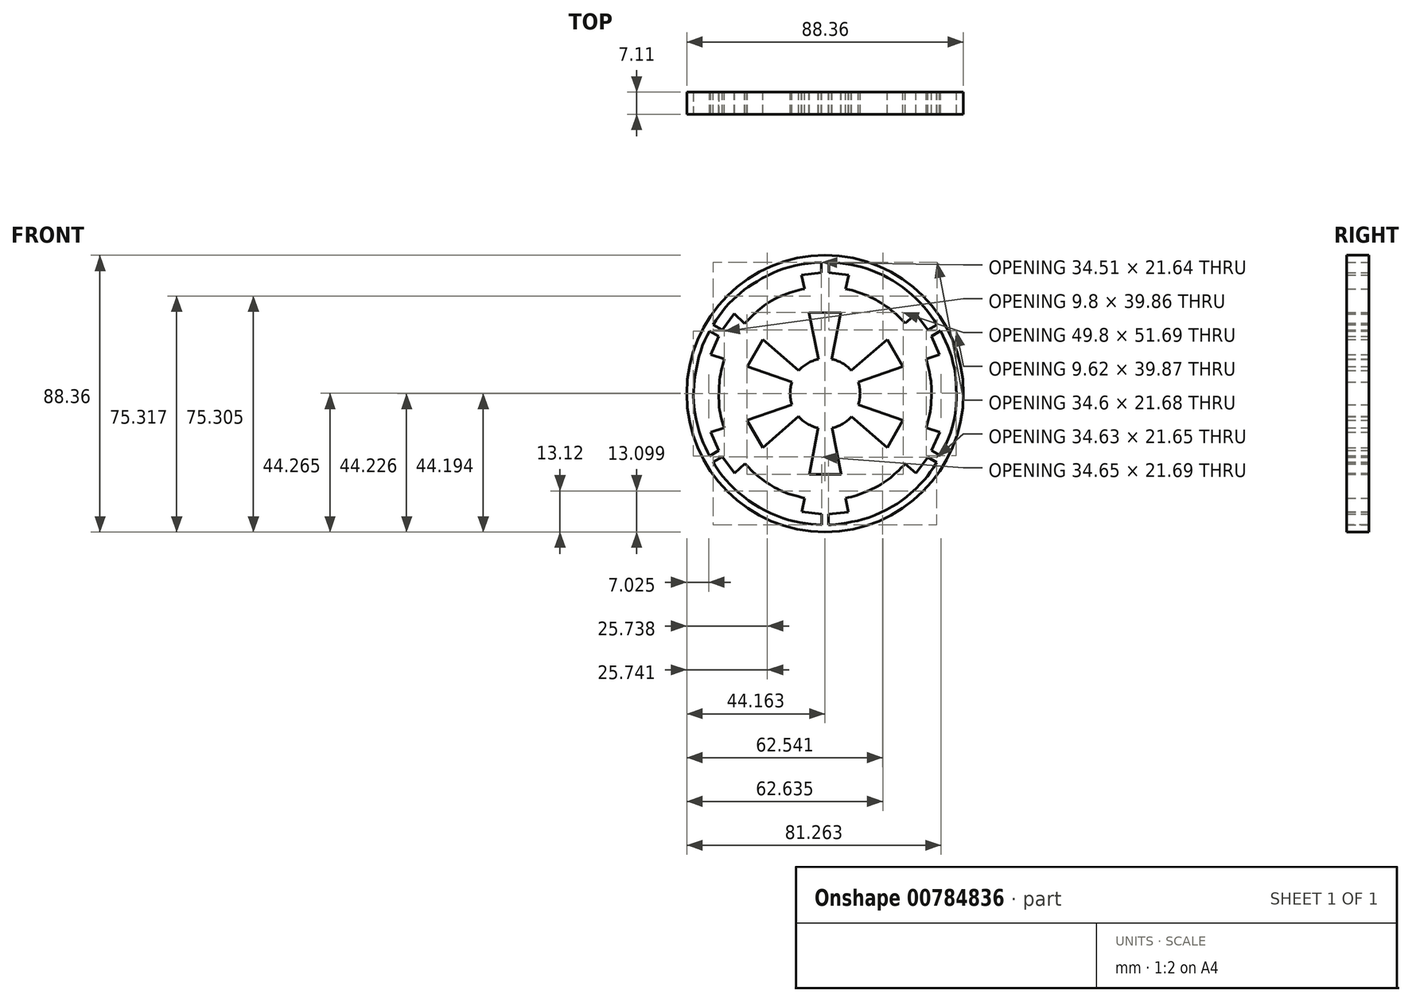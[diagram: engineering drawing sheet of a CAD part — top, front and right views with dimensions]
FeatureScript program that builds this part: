
annotation { "Feature Type Name" : "Feature", "Feature Type Description" : "" }
export const myFeature = defineFeature(function(context is Context, id is Id, definition is map)
    precondition{}
    {
        {
            var Q0;
            Q0=qCreatedBy(makeId("Front.planeOp"),FACE);
            var sketch = newSketch(context, id + "F0", { "sketchPlane" : qUnion([Q0])});
            skLineSegment(sketch, "E0", {"start": v(2.62, -13.26) * mm, "end": v(5.1, -25.8) * mm});
            skLineSegment(sketch, "E1", {"start": v(-2.6, -13.26) * mm, "end": v(-4.96, -25.83) * mm});
            skLineSegment(sketch, "E2", {"start": v(-4.96, -25.83) * mm, "end": v(5.1, -25.8) * mm});
            skLineSegment(sketch, "E3", {"start": v(-10.25, -8.8) * mm, "end": v(-19.88, -17.27) * mm});
            skLineSegment(sketch, "E4", {"start": v(-12.81, -4.3) * mm, "end": v(-24.92, -8.51) * mm});
            skLineSegment(sketch, "E5", {"start": v(-24.92, -8.51) * mm, "end": v(-19.88, -17.27) * mm});
            skLineSegment(sketch, "E6", {"start": v(12.8, -4.3) * mm, "end": v(24.88, -8.51) * mm});
            skLineSegment(sketch, "E7", {"start": v(10.2, -8.87) * mm, "end": v(19.9, -17.2) * mm});
            skLineSegment(sketch, "E8", {"start": v(19.9, -17.2) * mm, "end": v(24.88, -8.51) * mm});
            skLineSegment(sketch, "E9", {"start": v(12.77, 4.44) * mm, "end": v(24.88, 8.63) * mm});
            skLineSegment(sketch, "E10", {"start": v(10.14, 8.94) * mm, "end": v(19.81, 17.33) * mm});
            skLineSegment(sketch, "E11", {"start": v(19.81, 17.33) * mm, "end": v(24.88, 8.63) * mm});
            skLineSegment(sketch, "E12", {"start": v(2.56, 13.27) * mm, "end": v(5.03, 25.86) * mm});
            skLineSegment(sketch, "E13", {"start": v(-2.57, 13.27) * mm, "end": v(-5.14, 25.83) * mm});
            skLineSegment(sketch, "E14", {"start": v(-5.14, 25.83) * mm, "end": v(5.03, 25.86) * mm});
            skLineSegment(sketch, "E15", {"start": v(-10.19, 8.88) * mm, "end": v(-19.85, 17.32) * mm});
            skLineSegment(sketch, "E16", {"start": v(-12.77, 4.43) * mm, "end": v(-24.88, 8.62) * mm});
            skLineSegment(sketch, "E17", {"start": v(-24.88, 8.62) * mm, "end": v(-19.85, 17.32) * mm});
            skLineSegment(sketch, "E18", {"start": v(-1.19, 41.94) * mm, "end": v(-1.19, 38.6) * mm});
            skLineSegment(sketch, "E19", {"start": v(1.15, 41.98) * mm, "end": v(1.15, 38.6) * mm});
            skLineSegment(sketch, "E20", {"start": v(34, 18.3) * mm, "end": v(36.91, 20.02) * mm});
            skLineSegment(sketch, "E21", {"start": v(34, -18.17) * mm, "end": v(36.9, -19.85) * mm});
            skLineSegment(sketch, "E22", {"start": v(32.88, -20.26) * mm, "end": v(35.68, -21.93) * mm});
            skLineSegment(sketch, "E23", {"start": v(-32.81, -20.21) * mm, "end": v(-35.76, -21.87) * mm});
            skLineSegment(sketch, "E24", {"start": v(-36.86, -19.88) * mm, "end": v(-33.93, -18.2) * mm});
            skLineSegment(sketch, "E25", {"start": v(-36.87, 19.98) * mm, "end": v(-33.92, 18.32) * mm});
            skLineSegment(sketch, "E26", {"start": v(-35.7, 22.04) * mm, "end": v(-32.8, 20.3) * mm});
            skLineSegment(sketch, "E27", {"start": v(-33.92, 18.32) * mm, "end": v(-36.56, 12.47) * mm});
            skLineSegment(sketch, "E28", {"start": v(-36.56, 12.47) * mm, "end": v(-32.26, 11.04) * mm});
            skLineSegment(sketch, "E29", {"start": v(-32.8, 20.3) * mm, "end": v(-29, 25.5) * mm});
            skLineSegment(sketch, "E30", {"start": v(-29, 25.5) * mm, "end": v(-25.68, 22.43) * mm});
            skLineSegment(sketch, "E31", {"start": v(-33.93, -18.2) * mm, "end": v(-36.55, -12.33) * mm});
            skLineSegment(sketch, "E32", {"start": v(-36.55, -12.33) * mm, "end": v(-32.26, -10.87) * mm});
            skLineSegment(sketch, "E33", {"start": v(-32.81, -20.21) * mm, "end": v(-28.96, -25.37) * mm});
            skLineSegment(sketch, "E34", {"start": v(-28.96, -25.37) * mm, "end": v(-25.6, -22.34) * mm});
            skPoint(sketch, "E35.end.orphan", {"position": v(-1.27, -41.9) * mm});
            skPoint(sketch, "E35.start.orphan", {"position": v(-1.27, -38.52) * mm});
            skLineSegment(sketch, "E36", {"start": v(-1.12, -38.52) * mm, "end": v(-1.12, -41.9) * mm});
            skPoint(sketch, "E37.end.orphan", {"position": v(1.2, -41.9) * mm});
            skPoint(sketch, "E37.start.orphan", {"position": v(1.2, -38.52) * mm});
            skLineSegment(sketch, "E38", {"start": v(-1.12, -38.52) * mm, "end": v(-1.27, -38.52) * mm});
            skLineSegment(sketch, "E39", {"start": v(-1.12, -38.52) * mm, "end": v(-7.5, -37.75) * mm});
            skLineSegment(sketch, "E40", {"start": v(-7.5, -37.75) * mm, "end": v(-6.57, -33.33) * mm});
            skLineSegment(sketch, "E41", {"start": v(1.04, -38.52) * mm, "end": v(1.04, -41.9) * mm});
            skLineSegment(sketch, "E42", {"start": v(1.04, -38.52) * mm, "end": v(7.43, -37.82) * mm});
            skLineSegment(sketch, "E43", {"start": v(7.43, -37.82) * mm, "end": v(6.52, -33.4) * mm});
            skLineSegment(sketch, "E44", {"start": v(32.88, -20.26) * mm, "end": v(29.04, -25.4) * mm});
            skLineSegment(sketch, "E45", {"start": v(29.04, -25.4) * mm, "end": v(25.6, -22.45) * mm});
            skLineSegment(sketch, "E46", {"start": v(34, -18.17) * mm, "end": v(36.62, -12.34) * mm});
            skLineSegment(sketch, "E47", {"start": v(36.62, -12.34) * mm, "end": v(32.34, -10.9) * mm});
            skLineSegment(sketch, "E48", {"start": v(34, 18.3) * mm, "end": v(36.57, 12.42) * mm});
            skLineSegment(sketch, "E49", {"start": v(36.57, 12.42) * mm, "end": v(32.28, 11.02) * mm});
            skLineSegment(sketch, "E50", {"start": v(32.84, 20.3) * mm, "end": v(35.76, 22) * mm});
            skLineSegment(sketch, "E51", {"start": v(32.84, 20.3) * mm, "end": v(29, 25.44) * mm});
            skLineSegment(sketch, "E52", {"start": v(29, 25.44) * mm, "end": v(25.61, 22.47) * mm});
            skLineSegment(sketch, "E53", {"start": v(-1.19, 38.6) * mm, "end": v(-7.58, 37.87) * mm});
            skLineSegment(sketch, "E54", {"start": v(-7.58, 37.87) * mm, "end": v(-6.6, 33.44) * mm});
            skLineSegment(sketch, "E55", {"start": v(1.15, 38.6) * mm, "end": v(7.53, 37.86) * mm});
            skLineSegment(sketch, "E56", {"start": v(7.53, 37.86) * mm, "end": v(6.59, 33.4) * mm});
            skFitSpline(sketch, "E57", {"points": [v(-32.26, -10.87) * mm, v(-33.66, -5.43) * mm, v(-33.9, 0) * mm, v(-33.54, 5.46) * mm, v(-32.26, 11.04) * mm], "startDerivative": vector(-6.71, 21.57) * mm, "endDerivative": vector(5.92, 22) * mm});
            skFitSpline(sketch, "E58", {"points": [v(-25.68, 22.43) * mm, v(-21.68, 26.27) * mm, v(-17.69, 29.3) * mm, v(-11.76, 32.08) * mm, v(-6.6, 33.44) * mm], "startDerivative": vector(16.19, 16.08) * mm, "endDerivative": vector(20.55, 4.51) * mm});
            skFitSpline(sketch, "E59", {"points": [v(-25.6, -22.34) * mm, v(-22.09, -25.83) * mm, v(-17.7, -29) * mm, v(-12.88, -31.51) * mm, v(-6.57, -33.33) * mm], "startDerivative": vector(14.21, -15.18) * mm, "endDerivative": vector(24.22, -5.87) * mm});
            skFitSpline(sketch, "E60", {"points": [v(6.52, -33.4) * mm, v(10.43, -32.34) * mm, v(15.18, -30.36) * mm, v(19.6, -27.8) * mm, v(22.48, -25.4) * mm, v(25.6, -22.45) * mm], "startDerivative": vector(20.1, 4.76) * mm, "endDerivative": vector(16.26, 15.48) * mm});
            skFitSpline(sketch, "E61", {"points": [v(32.34, -10.9) * mm, v(33.58, -5.53) * mm, v(34, 0) * mm, v(34, 2.2) * mm, v(33.5, 5.84) * mm, v(32.28, 11.02) * mm], "startDerivative": vector(6.39, 22.77) * mm, "endDerivative": vector(-6.09, 23.91) * mm});
            skFitSpline(sketch, "E62", {"points": [v(25.61, 22.47) * mm, v(22.13, 25.84) * mm, v(17.85, 28.97) * mm, v(14.13, 30.98) * mm, v(8.7, 32.92) * mm, v(6.59, 33.4) * mm], "startDerivative": vector(-15.56, 16.18) * mm, "endDerivative": vector(-12.9, 2.5) * mm});
            skFitSpline(sketch, "E63", {"points": [v(-35.7, 22.04) * mm, v(-32.26, 27.01) * mm, v(-27.88, 31.44) * mm, v(-23.76, 34.6) * mm, v(-17.69, 38.04) * mm, v(-10.42, 40.68) * mm, v(-1.19, 41.94) * mm], "startDerivative": vector(20.42, 32.39) * mm, "endDerivative": vector(49.13, 4.55) * mm});
            skFitSpline(sketch, "E64", {"points": [v(-36.87, 19.98) * mm, v(-39.57, 14.2) * mm, v(-41.37, 6.42) * mm, v(-42.05, 0) * mm, v(-41.46, -6.76) * mm, v(-39.1, -15.28) * mm, v(-36.86, -19.88) * mm], "startDerivative": vector(-18.3, -33.84) * mm, "endDerivative": vector(15.88, -28.7) * mm});
            skFitSpline(sketch, "E65", {"points": [v(-35.76, -21.87) * mm, v(-34.07, -24.57) * mm, v(-31.3, -27.99) * mm, v(-26.23, -32.77) * mm, v(-19.88, -36.91) * mm, v(-12.82, -39.98) * mm, v(-6.67, -41.35) * mm, v(-1.12, -41.9) * mm], "startDerivative": vector(15, -25.38) * mm, "endDerivative": vector(39.5, -3.13) * mm});
            skPoint(sketch, "E66.1.internal.orphan", {"position": v(2.81, -41.9) * mm});
            skPoint(sketch, "E66.5.internal.orphan", {"position": v(24.54, -34.16) * mm});
            skPoint(sketch, "E66.7.internal.orphan", {"position": v(32.73, -26.55) * mm});
            skFitSpline(sketch, "E67", {"points": [v(1.04, -41.9) * mm, v(2.34, -41.9) * mm, v(6.1, -41.4) * mm, v(9.9, -40.67) * mm, v(14.23, -39.47) * mm, v(19.53, -37.12) * mm, v(23.68, -34.68) * mm, v(27.2, -31.99) * mm, v(31.17, -28.05) * mm, v(33.22, -25.61) * mm, v(35.68, -21.93) * mm], "startDerivative": vector(19.64, -0.97) * mm, "endDerivative": vector(24.32, 37.94) * mm});
            skFitSpline(sketch, "E68", {"points": [v(1.15, 41.98) * mm, v(8, 41.23) * mm, v(14.33, 39.52) * mm, v(20.7, 36.61) * mm, v(26.6, 32.55) * mm, v(32.17, 27.03) * mm, v(35.76, 22) * mm], "startDerivative": vector(41.76, -3.24) * mm, "endDerivative": vector(20.77, -31.79) * mm});
            skFitSpline(sketch, "E69", {"points": [v(36.91, 20.02) * mm, v(39.69, 13.75) * mm, v(41.52, 6.68) * mm, v(41.88, 1.39) * mm, v(41.79, -4.77) * mm, v(40.16, -12.25) * mm, v(36.9, -19.85) * mm], "startDerivative": vector(17.68, -36.35) * mm, "endDerivative": vector(-19.56, -41.17) * mm});
            skCircle(sketch, "E70", {"center": v(0, 0) * mm, "radius": 44.18 * mm});
            skLineSegment(sketch, "E71", {"start": v(10.56, 3.67) * mm, "end": v(10.5, 3.65) * mm});
            skLineSegment(sketch, "E72", {"start": v(8.37, 7.4) * mm, "end": v(8.32, 7.36) * mm});
            skLineSegment(sketch, "E73", {"start": v(-2.1, 10.98) * mm, "end": v(-2.08, 10.92) * mm});
            skLineSegment(sketch, "E74", {"start": v(2.12, 10.97) * mm, "end": v(2.1, 10.91) * mm});
            skLineSegment(sketch, "E75", {"start": v(-8.42, 7.34) * mm, "end": v(-8.38, 7.3) * mm});
            skLineSegment(sketch, "E76", {"start": v(-10.56, 3.66) * mm, "end": v(-10.5, 3.64) * mm});
            skLineSegment(sketch, "E77", {"start": v(-10.6, -3.52) * mm, "end": v(-10.55, -3.5) * mm});
            skLineSegment(sketch, "E78", {"start": v(-8.5, -7.26) * mm, "end": v(-8.45, -7.22) * mm});
            skLineSegment(sketch, "E79", {"start": v(-2.16, -10.96) * mm, "end": v(-2.15, -10.9) * mm});
            skLineSegment(sketch, "E80", {"start": v(2.17, -10.96) * mm, "end": v(2.16, -10.9) * mm});
            skLineSegment(sketch, "E81", {"start": v(8.42, -7.35) * mm, "end": v(8.37, -7.3) * mm});
            skLineSegment(sketch, "E82", {"start": v(10.6, -3.54) * mm, "end": v(10.54, -3.52) * mm});
            skCircle(sketch, "E83", {"center": v(0, 0) * mm, "radius": 11.18 * mm});
            skLineSegment(sketch, "E84", {"start": v(-10.19, 8.88) * mm, "end": v(-8.42, 7.34) * mm});
            skLineSegment(sketch, "E85", {"start": v(-12.77, 4.43) * mm, "end": v(-10.5, 3.64) * mm});
            skLineSegment(sketch, "E86", {"start": v(-12.81, -4.3) * mm, "end": v(-10.55, -3.5) * mm});
            skLineSegment(sketch, "E87", {"start": v(-10.25, -8.8) * mm, "end": v(-8.45, -7.22) * mm});
            skLineSegment(sketch, "E88", {"start": v(-2.6, -13.26) * mm, "end": v(-2.15, -10.9) * mm});
            skLineSegment(sketch, "E89", {"start": v(2.62, -13.26) * mm, "end": v(2.17, -10.96) * mm});
            skLineSegment(sketch, "E90", {"start": v(10.2, -8.87) * mm, "end": v(8.42, -7.35) * mm});
            skLineSegment(sketch, "E91", {"start": v(12.8, -4.3) * mm, "end": v(10.6, -3.54) * mm});
            skLineSegment(sketch, "E92", {"start": v(12.77, 4.44) * mm, "end": v(10.56, 3.67) * mm});
            skLineSegment(sketch, "E93", {"start": v(10.14, 8.94) * mm, "end": v(8.37, 7.4) * mm});
            skLineSegment(sketch, "E94", {"start": v(2.56, 13.27) * mm, "end": v(2.12, 10.97) * mm});
            skLineSegment(sketch, "E95", {"start": v(-2.57, 13.27) * mm, "end": v(-2.08, 10.92) * mm});
            skSolve(sketch);
        }
        {
            var Q0;
            Q0 = qSketchRegion(id + "F0", true);
            extrude(context, id + "F1", {"entities" : qUnion([Q0]), "depth" : 7.11 * mm, "offsetDistance" : 25.4 * mm});
        }
    });
